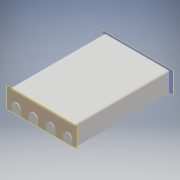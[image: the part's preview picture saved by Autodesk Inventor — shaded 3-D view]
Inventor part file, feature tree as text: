
AUTODESK INVENTOR PART (.ipt)
format: ipt  version: 2018 (Build 220112000, 112)  size: 190,976 bytes
history: native  units: mm
features: other x7, projected_geometry x5, extrude x3, sketch x3, plane x2, fillet x1
ambient origin geometry x8: Origin, YZ Plane, XZ Plane, XY Plane, X Axis, Y Axis, Z Axis, Center Point
bodies: Body1 (feature_tree), Body2 (feature_tree), Body3 (feature_tree)
feature tree (21):
  other  "Sólido1"
  extrude  "Extrusión1"  TaperAngle=90.0deg  [1 undecoded]
  plane  "Plano de trabajo1"
  extrude  "Extrusión2"  Depth=0.3mm TaperAngle=0.0deg
  plane  "Plano de trabajo2"
  extrude  "Extrusión3"  Depth=0.3mm TaperAngle=0.0deg
  fillet  "Empalme1"  Radius=0.05mm
  other  "Edición directa1"
  other  "Edición directa2"
  sketch  "Boceto1"  dims[d0=0.6mm d1=0.0mm d2=90.0deg]
  sketch  "Boceto2"  dims[d3=40.0mm d5=0.53mm d6=10.0mm d8=10.0mm d10=0.3mm d11=0.0mm]
  other  "Sólido2"
  sketch  "Boceto3"  dims[d12=90.0deg d13=0.3mm d14=0.0mm d15=0.05mm d16=0.0mm d17=0.0mm d18=0.02mm d19=0.0mm d20=0.0mm d21=0.02mm]
  projected_geometry  "Contorno proyectado1"
  projected_geometry  "Contorno proyectado2"
  projected_geometry  "Contorno proyectado3"
  projected_geometry  "Contorno proyectado4"
  projected_geometry  "Contorno proyectado5"
  other  "Sólido3"
  other  "Desplazar1"
  other  "Desplazar2"
note: 1 required parameter value undecoded (feature->parameter linkage not recoverable at this tier; creation-order binding heuristic only, values carry confidence <= 0.55)
